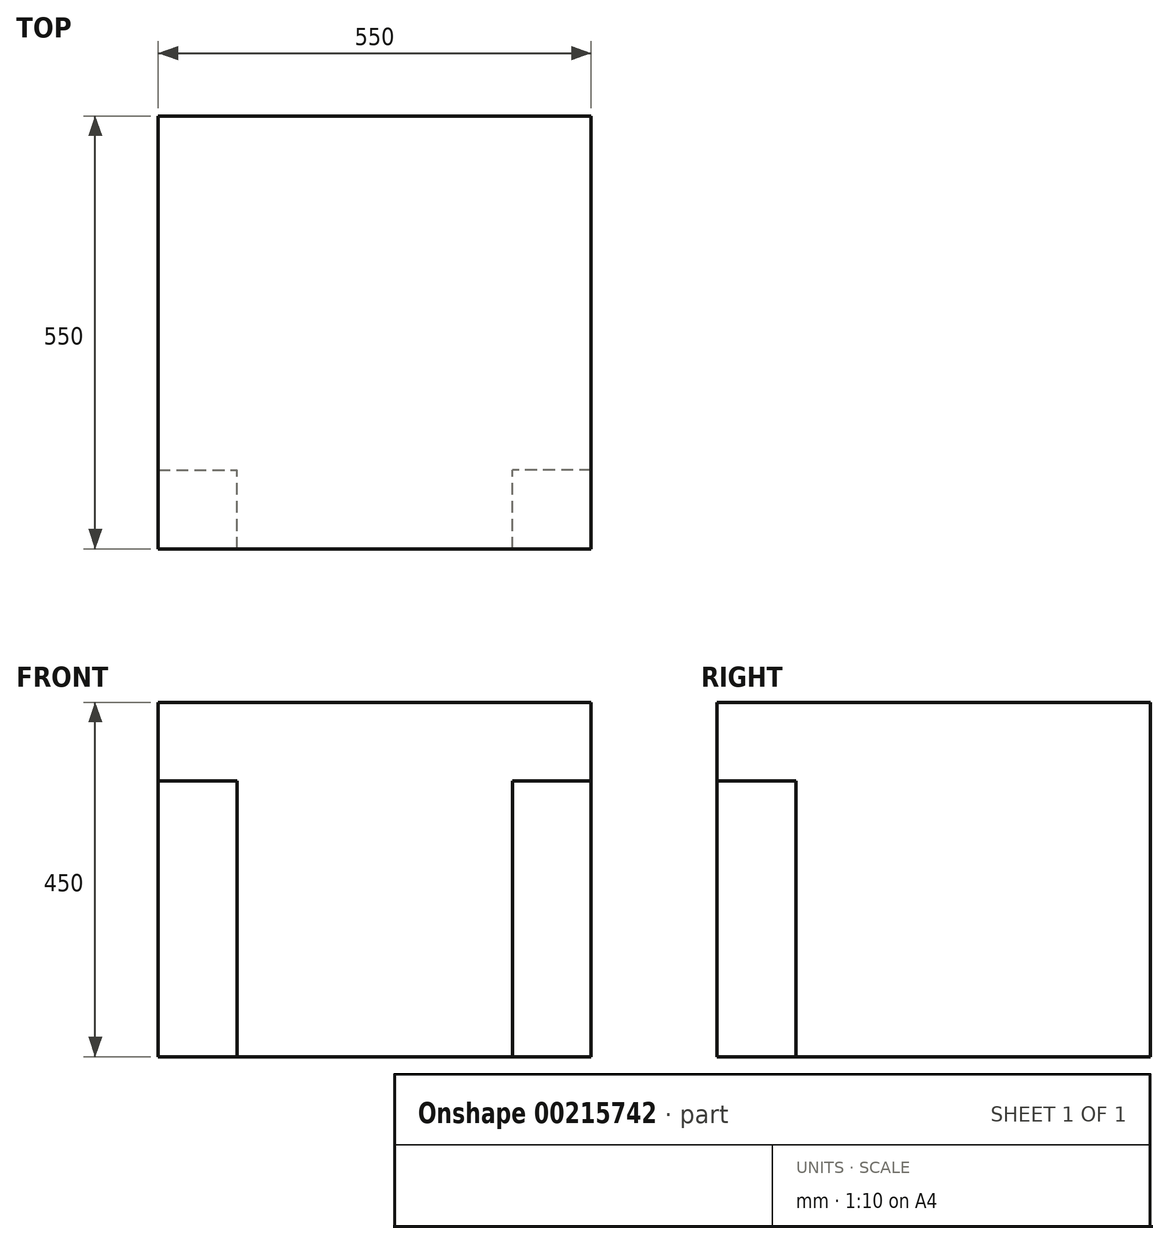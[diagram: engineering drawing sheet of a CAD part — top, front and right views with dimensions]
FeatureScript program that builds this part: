
annotation { "Feature Type Name" : "Feature", "Feature Type Description" : "" }
export const myFeature = defineFeature(function(context is Context, id is Id, definition is map)
    precondition{}
    {
        {
            var Q0;
            Q0=qCreatedBy(makeId("Top.planeOp"),FACE);
            var sketch = newSketch(context, id + "F0", { "sketchPlane" : qUnion([Q0])});
            skLineSegment(sketch, "E0.bottom", {"start": v(0, 0) * mm, "end": v(550, 0) * mm});
            skLineSegment(sketch, "E0.top", {"start": v(0, 550) * mm, "end": v(550, 550) * mm});
            skLineSegment(sketch, "E0.left", {"start": v(0, 0) * mm, "end": v(0, 550) * mm});
            skLineSegment(sketch, "E0.right", {"start": v(550, 0) * mm, "end": v(550, 550) * mm});
            skSolve(sketch);
        }
        {
            var Q0;
            Q0 = qSketchRegion(id + "F0", true);
            extrude(context, id + "F1", {"entities" : qUnion([Q0]), "oppositeDirection" : true, "depth" : 450 * mm});
        }
        {
            var Q0;
            Q0=makeQuery(id+"F1.opExtrude","CAP_FACE",FACE,{"disambiguationData":[OSD([sQuery(id+"F0.wireOp",EDGE,"E0.bottom"),sQuery(id+"F0.wireOp",EDGE,"E0.top"),sQuery(id+"F0.wireOp",EDGE,"E0.left"),sQuery(id+"F0.wireOp",EDGE,"E0.right")])],"isStart":false});
            var sketch = newSketch(context, id + "F2", { "sketchPlane" : qUnion([Q0])});
            skLineSegment(sketch, "E1.bottom", {"start": v(0, 0) * mm, "end": v(550, 0) * mm});
            skLineSegment(sketch, "E1.top", {"start": v(0, -550) * mm, "end": v(550, -550) * mm});
            skLineSegment(sketch, "E1.left", {"start": v(0, 0) * mm, "end": v(0, -550) * mm});
            skLineSegment(sketch, "E1.right", {"start": v(550, 0) * mm, "end": v(550, -550) * mm});
            skLineSegment(sketch, "E2.bottom", {"start": v(0, 0) * mm, "end": v(100, 0) * mm});
            skLineSegment(sketch, "E2.top", {"start": v(0, -100) * mm, "end": v(100, -100) * mm});
            skLineSegment(sketch, "E2.left", {"start": v(0, 0) * mm, "end": v(0, -100) * mm});
            skLineSegment(sketch, "E2.right", {"start": v(100, 0) * mm, "end": v(100, -100) * mm});
            skLineSegment(sketch, "E3.bottom", {"start": v(550, 0) * mm, "end": v(450, 0) * mm});
            skLineSegment(sketch, "E3.top", {"start": v(550, -100) * mm, "end": v(450, -100) * mm});
            skLineSegment(sketch, "E3.left", {"start": v(550, 0) * mm, "end": v(550, -100) * mm});
            skLineSegment(sketch, "E3.right", {"start": v(450, 0) * mm, "end": v(450, -100) * mm});
            skLineSegment(sketch, "E4.bottom", {"start": v(550, -550) * mm, "end": v(450, -550) * mm});
            skLineSegment(sketch, "E4.top", {"start": v(550, -450) * mm, "end": v(450, -450) * mm});
            skLineSegment(sketch, "E4.left", {"start": v(550, -550) * mm, "end": v(550, -450) * mm});
            skLineSegment(sketch, "E4.right", {"start": v(450, -550) * mm, "end": v(450, -450) * mm});
            skLineSegment(sketch, "E5.bottom", {"start": v(0, -550) * mm, "end": v(100, -550) * mm});
            skLineSegment(sketch, "E5.top", {"start": v(0, -450) * mm, "end": v(100, -450) * mm});
            skLineSegment(sketch, "E5.left", {"start": v(0, -550) * mm, "end": v(0, -450) * mm});
            skLineSegment(sketch, "E5.right", {"start": v(100, -550) * mm, "end": v(100, -450) * mm});
            skSolve(sketch);
        }
        {
            var Q0;
            Q0=makeQuery(id+"F2.imprint","IMPRINT",FACE,{"disambiguationData":[TD([[makeQuery(id+"F2.imprint","IMPRINT",EDGE,{"derivedFrom":sQuery(id+"F2.wireOp",EDGE,"E1.bottom")}),-1.0]])]});
            extrude(context, id + "F3", {"entities" : qUnion([Q0]), "operationType" : NewBodyOperationType.REMOVE, "oppositeDirection" : true, "depth" : 350 * mm});
        }
    });
